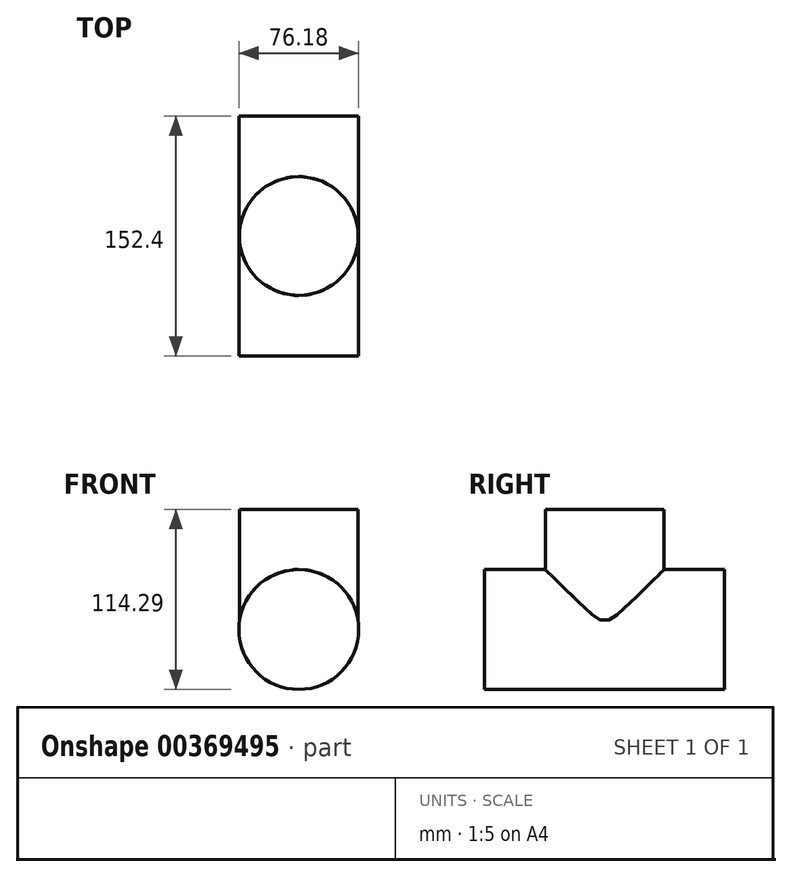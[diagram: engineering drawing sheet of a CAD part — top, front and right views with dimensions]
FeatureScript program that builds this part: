
annotation { "Feature Type Name" : "Feature", "Feature Type Description" : "" }
export const myFeature = defineFeature(function(context is Context, id is Id, definition is map)
    precondition{}
    {
        {
            var Q0;
            Q0=qCreatedBy(makeId("Front.planeOp"),FACE);
            var sketch = newSketch(context, id + "F0", { "sketchPlane" : qUnion([Q0])});
            skCircle(sketch, "E0", {"center": v(0, 0) * mm, "radius": 38.1 * mm});
            skSolve(sketch);
        }
        {
            var Q0;
            Q0=makeQuery(id+"F0.imprint","IMPRINT",FACE,{"disambiguationData":[TD([[makeQuery(id+"F0.imprint","IMPRINT",EDGE,{"derivedFrom":sQuery(id+"F0.wireOp",EDGE,"E0")}),1.0]])]});
            extrude(context, id + "F1", {"entities" : qUnion([Q0]), "depth" : 76.2 * mm});
        }
        {
            var Q0;
            Q0 = qSketchRegion(id + "F0", true);
            var Q1;
            Q1=makeQuery(id+"F1.opExtrude","CAP_FACE",FACE,{"disambiguationData":[OSD([sQuery(id+"F0.wireOp",EDGE,"E0")])],"isStart":true});
            extrude(context, id + "F2", {"entities" : qUnion([Q0, Q1]), "operationType" : NewBodyOperationType.ADD, "oppositeDirection" : true, "depth" : 76.2 * mm});
        }
        {
            var Q0;
            Q0=qCreatedBy(makeId("Top.planeOp"),FACE);
            var sketch = newSketch(context, id + "F3", { "sketchPlane" : qUnion([Q0])});
            skCircle(sketch, "E1", {"center": v(0, 0) * mm, "radius": 37.72 * mm});
            skSolve(sketch);
        }
        {
            var Q0;
            Q0=makeQuery(id+"F3.imprint","IMPRINT",FACE,{"disambiguationData":[TD([[makeQuery(id+"F3.imprint","IMPRINT",EDGE,{"derivedFrom":sQuery(id+"F3.wireOp",EDGE,"E1")}),1.0]])]});
            extrude(context, id + "F4", {"entities" : qUnion([Q0]), "operationType" : NewBodyOperationType.ADD, "depth" : 76.2 * mm});
        }
    });
